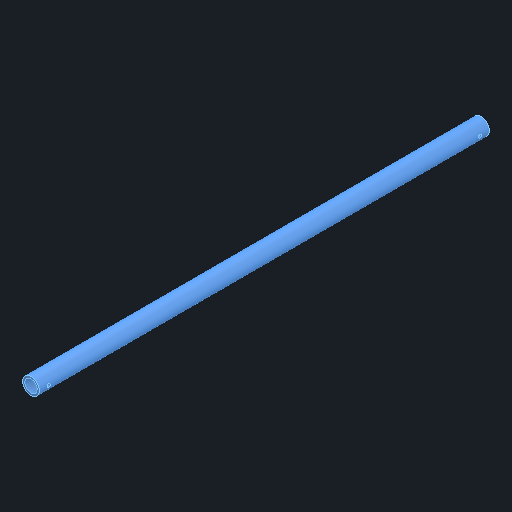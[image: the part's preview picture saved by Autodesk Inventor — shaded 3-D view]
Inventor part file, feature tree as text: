
AUTODESK INVENTOR PART (.ipt)
format: ipt  version: 2024 (Build 280153000, 153)  size: 103,936 bytes
history: native  units: in
note: dims shown in document units (in); Inventor stores cm internally (conversion verified against a paired STEP export)
features: mirror x1
ambient origin geometry x8: Origin, YZ Plane, XZ Plane, XY Plane, X Axis, Y Axis, Z Axis, Center Point
bodies: Solid1 (feature_tree)
feature tree (1):
  mirror  "Mirror1"
